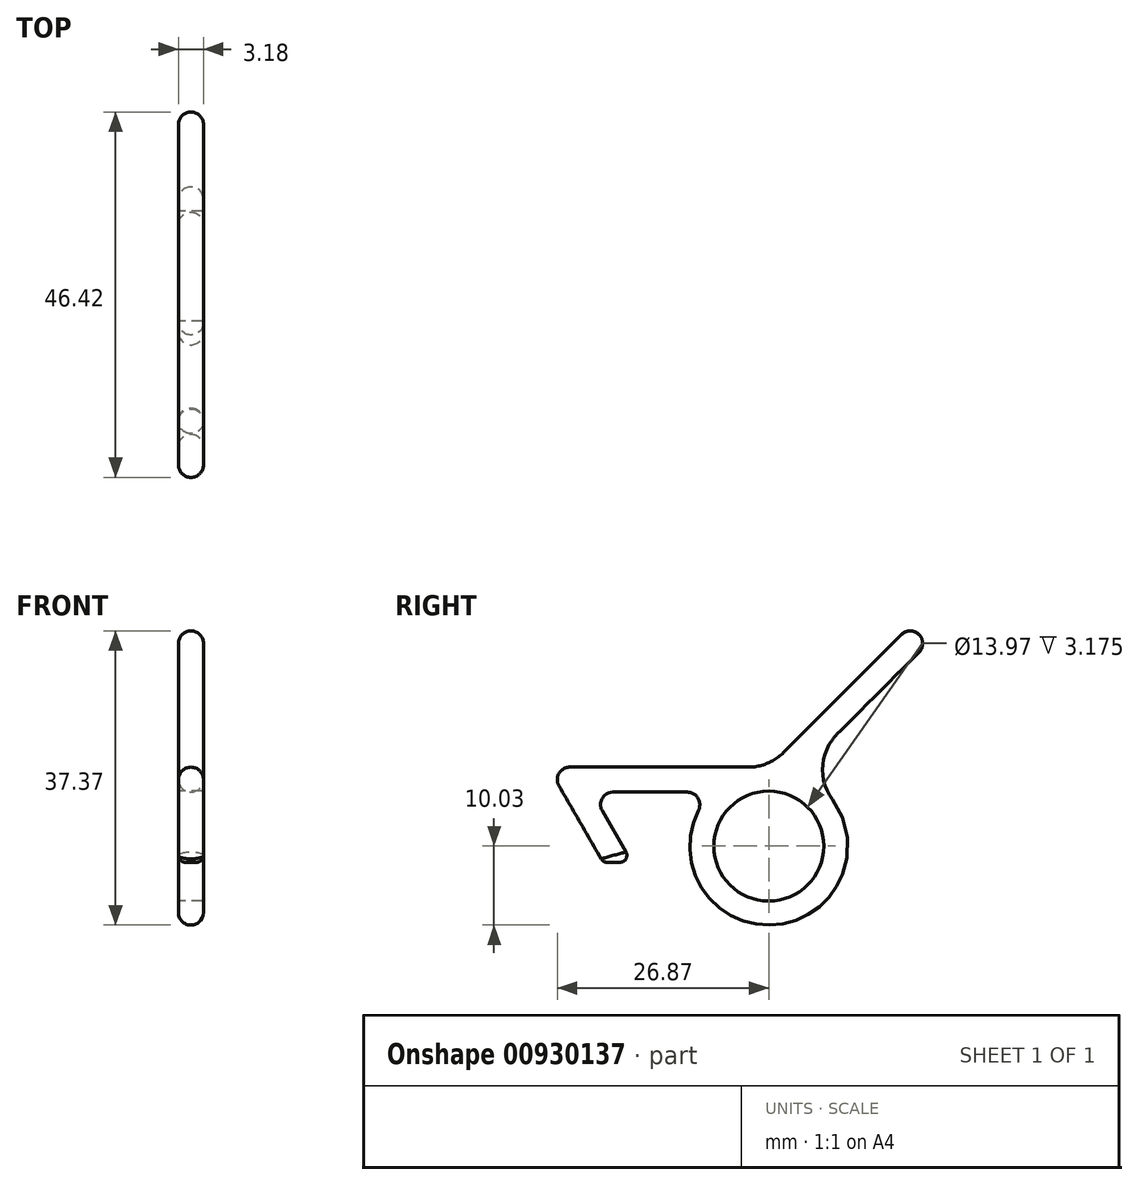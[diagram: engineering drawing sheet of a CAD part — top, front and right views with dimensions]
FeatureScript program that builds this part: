
annotation { "Feature Type Name" : "Feature", "Feature Type Description" : "" }
export const myFeature = defineFeature(function(context is Context, id is Id, definition is map)
    precondition{}
    {
        {
            var Q0;
            Q0=qCreatedBy(makeId("Right.planeOp"),FACE);
            var sketch = newSketch(context, id + "F0", { "sketchPlane" : qUnion([Q0])});
            skCircle(sketch, "E0", {"center": v(0, 0) * mm, "radius": 6.99 * mm});
            skArc(sketch, "E1.0", {"start": v(-8.94, 4.55) * mm, "mid": v(0.83, -10) * mm, "end": v(8.07, 5.96) * mm});
            skLineSegment(sketch, "E2", {"start": v(-2.63, 10.03) * mm, "end": v(-25.28, 10.03) * mm});
            skLineSegment(sketch, "E3", {"start": v(-26.66, 7.65) * mm, "end": v(-21.05, -2.07) * mm});
            skLineSegment(sketch, "E4", {"start": v(-21.05, -2.07) * mm, "end": v(-17.38, -2.07) * mm});
            skLineSegment(sketch, "E5", {"start": v(-17.38, -2.07) * mm, "end": v(-21.16, 4.48) * mm});
            skLineSegment(sketch, "E6", {"start": v(-19.78, 6.86) * mm, "end": v(-10.36, 6.86) * mm});
            skPoint(sketch, "E7.orphan", {"position": v(0, 6.86) * mm});
            skPoint(sketch, "E8.visualSharp", {"position": v(-7.32, 6.86) * mm});
            skLineSegment(sketch, "E9", {"start": v(1.86, 11.9) * mm, "end": v(17.96, 28) * mm});
            skLineSegment(sketch, "E10", {"start": v(17.96, 28) * mm, "end": v(20.2, 25.75) * mm});
            skLineSegment(sketch, "E11", {"start": v(20.2, 25.75) * mm, "end": v(8.68, 14.23) * mm});
            skPoint(sketch, "E12.visualSharp", {"position": v(0, 10.03) * mm});
            skArc(sketch, "E12.filletArc", {"start": v(-2.63, 10.03) * mm, "mid": v(-0.2, 10.52) * mm, "end": v(1.86, 11.9) * mm});
            skPoint(sketch, "E13.visualSharp", {"position": v(3.76, 9.3) * mm});
            skArc(sketch, "E13.filletArc", {"start": v(8.68, 14.23) * mm, "mid": v(6.84, 10.2) * mm, "end": v(8.07, 5.96) * mm});
            skPoint(sketch, "E14.visualSharp", {"position": v(-28.03, 10.03) * mm});
            skArc(sketch, "E14.filletArc", {"start": v(-25.28, 10.03) * mm, "mid": v(-26.66, 9.24) * mm, "end": v(-26.66, 7.65) * mm});
            skPoint(sketch, "E15.visualSharp", {"position": v(-22.53, 6.86) * mm});
            skArc(sketch, "E15.filletArc", {"start": v(-19.78, 6.86) * mm, "mid": v(-21.16, 6.06) * mm, "end": v(-21.16, 4.48) * mm});
            skArc(sketch, "E16.filletArc", {"start": v(-8.94, 4.55) * mm, "mid": v(-9, 6.1) * mm, "end": v(-10.36, 6.86) * mm});
            skSolve(sketch);
        }
        {
            var Q0;
            Q0=makeQuery(id+"F0.imprint","IMPRINT",FACE,{"disambiguationData":[TD([[makeQuery(id+"F0.imprint","IMPRINT",EDGE,{"derivedFrom":sQuery(id+"F0.wireOp",EDGE,"E0")}),-1.0]])]});
            extrude(context, id + "F1", {"entities" : qUnion([Q0]), "depth" : 3.17 * mm, "offsetDistance" : 25.4 * mm});
        }
        {
            var Q0;
            Q0=makeQuery(id+"F1.opExtrude","CAP_EDGE",EDGE,{"disambiguationData":[OSD([sQuery(id+"F0.wireOp",EDGE,"E3")])],"isStart":false});
            var Q1;
            Q1=makeQuery(id+"F1.opExtrude","CAP_EDGE",EDGE,{"disambiguationData":[OSD([sQuery(id+"F0.wireOp",EDGE,"E3")])],"isStart":true});
            var Q2;
            Q2=makeQuery(id+"F1.opExtrude","CAP_EDGE",EDGE,{"disambiguationData":[OSD([sQuery(id+"F0.wireOp",EDGE,"E5")])],"isStart":true});
            var Q3;
            Q3=makeQuery(id+"F1.opExtrude","CAP_EDGE",EDGE,{"disambiguationData":[OSD([sQuery(id+"F0.wireOp",EDGE,"E5")])],"isStart":false});
            fillet(context, id + "F2", {"entities" : qUnion([Q0, Q1, Q2, Q3]), "radius" : 1.59 * mm, "tangentPropagation" : true, "allowEdgeOverflow" : false});
        }
        {
            var Q0;
            Q0=makeQuery(id+"F2.opFillet","BLEND_EDGE",EDGE,{"blendedFrom":[makeQuery(id+"F1.opExtrude","CAP_EDGE",EDGE,{"disambiguationData":[OSD([sQuery(id+"F0.wireOp",EDGE,"E9")])],"isStart":true}),makeQuery(id+"F1.opExtrude","SWEPT_FACE",FACE,{"disambiguationData":[OSD([sQuery(id+"F0.wireOp",EDGE,"E10")])]})],"blendedInto":[makeQuery(id+"F1.opExtrude","SWEPT_FACE",FACE,{"disambiguationData":[OSD([sQuery(id+"F0.wireOp",EDGE,"E10")])]})]});
            fillet(context, id + "F3", {"entities" : qUnion([Q0]), "radius" : 1.59 * mm, "tangentPropagation" : true, "allowEdgeOverflow" : false});
        }
        {
            var Q0;
            Q0=makeQuery(id+"F2.opFillet","BLEND_EDGE",EDGE,{"blendedFrom":[makeQuery(id+"F1.opExtrude","CAP_EDGE",EDGE,{"disambiguationData":[OSD([sQuery(id+"F0.wireOp",EDGE,"E3")])],"isStart":true}),makeQuery(id+"F1.opExtrude","SWEPT_FACE",FACE,{"disambiguationData":[OSD([sQuery(id+"F0.wireOp",EDGE,"E4")])]})],"blendedInto":[makeQuery(id+"F1.opExtrude","SWEPT_FACE",FACE,{"disambiguationData":[OSD([sQuery(id+"F0.wireOp",EDGE,"E4")])]})]});
            fillet(context, id + "F4", {"entities" : qUnion([Q0]), "radius" : 0.89 * mm, "tangentPropagation" : true, "allowEdgeOverflow" : false});
        }
    });
